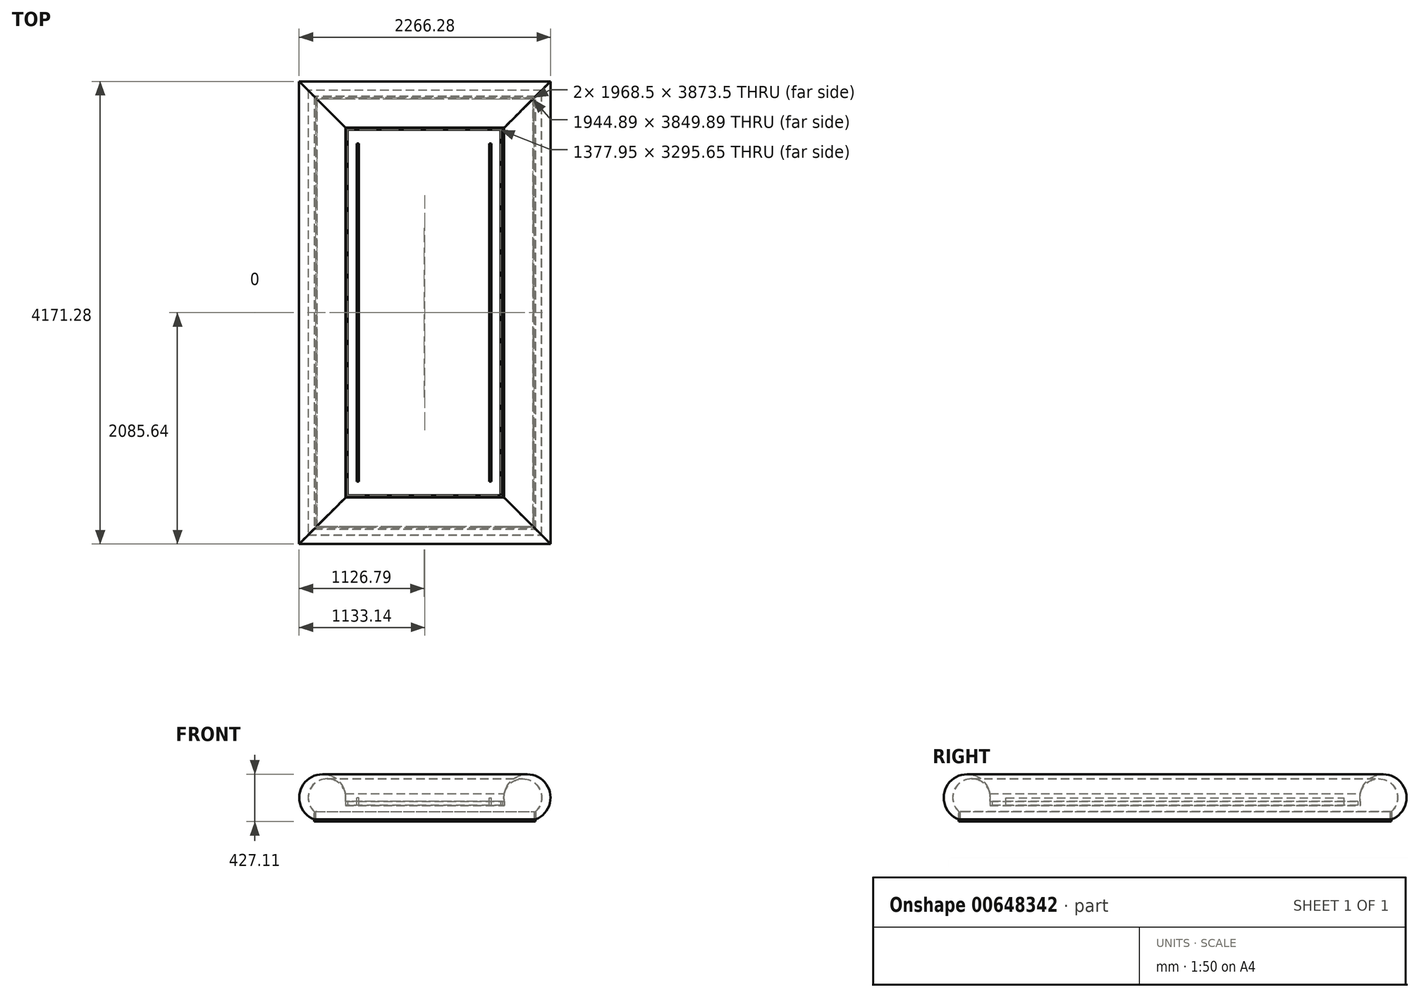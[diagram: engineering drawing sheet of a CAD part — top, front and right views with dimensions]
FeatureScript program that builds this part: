
annotation { "Feature Type Name" : "Feature", "Feature Type Description" : "" }
export const myFeature = defineFeature(function(context is Context, id is Id, definition is map)
    precondition{}
    {
        {
            var Q0;
            Q0=qCreatedBy(makeId("Front.planeOp"),FACE);
            var sketch = newSketch(context, id + "F0", { "sketchPlane" : qUnion([Q0])});
            skLineSegment(sketch, "E0.bottom", {"start": v(0, 0) * mm, "end": v(12.7, 0) * mm});
            skLineSegment(sketch, "E0.top", {"start": v(0, -88.9) * mm, "end": v(12.7, -88.9) * mm});
            skLineSegment(sketch, "E0.left", {"start": v(0, 0) * mm, "end": v(0, -88.9) * mm});
            skLineSegment(sketch, "E0.right", {"start": v(12.7, 0) * mm, "end": v(12.7, -88.9) * mm});
            skLineSegment(sketch, "E1.bottom", {"start": v(301.63, 57.15) * mm, "end": v(282.58, 57.15) * mm});
            skLineSegment(sketch, "E1.top", {"start": v(301.63, 92.07) * mm, "end": v(282.58, 92.07) * mm});
            skLineSegment(sketch, "E1.left", {"start": v(301.63, 57.15) * mm, "end": v(301.63, 92.08) * mm});
            skLineSegment(sketch, "E1.right", {"start": v(282.58, 57.15) * mm, "end": v(282.58, 92.08) * mm});
            skPoint(sketch, "E1.middle", {"position": v(292.1, 74.61) * mm});
            skArc(sketch, "E2", {"start": v(282.58, 92.08) * mm, "mid": v(61.68, 290.36) * mm, "end": v(0, 0) * mm});
            skLineSegment(sketch, "E3.bottom", {"start": v(403.23, 57.15) * mm, "end": v(384.18, 57.15) * mm});
            skLineSegment(sketch, "E3.top", {"start": v(403.23, 123.83) * mm, "end": v(384.18, 123.83) * mm});
            skLineSegment(sketch, "E3.left", {"start": v(403.23, 57.15) * mm, "end": v(403.23, 123.83) * mm});
            skLineSegment(sketch, "E3.right", {"start": v(384.18, 57.15) * mm, "end": v(384.18, 123.83) * mm});
            skPoint(sketch, "E3.middle", {"position": v(393.7, 90.49) * mm});
            skLineSegment(sketch, "E4", {"start": v(-111.56, 298.8) * mm, "end": v(114.8, 298.8) * mm});
            skArc(sketch, "E5", {"start": v(282.58, 92.08) * mm, "mid": v(-30.16, 310.3) * mm, "end": v(0, -69.85) * mm});
            skPoint(sketch, "E6", {"position": v(0, -44.45) * mm});
            skLineSegment(sketch, "E7", {"start": v(74.68, 338.21) * mm, "end": v(-177.95, 338.21) * mm});
            skLineSegment(sketch, "E8", {"start": v(990.6, 508.95) * mm, "end": v(990.6, -432.45) * mm, "construction": true});
            skLineSegment(sketch, "E9", {"start": v(12.7, 0) * mm, "end": v(282.58, 57.15) * mm});
            skLineSegment(sketch, "E10.MirrorCS", {"start": v(1679.58, 92.07) * mm, "end": v(1698.62, 92.07) * mm});
            skLineSegment(sketch, "E11.MirrorCS", {"start": v(1679.58, 57.15) * mm, "end": v(1679.58, 92.07) * mm});
            skLineSegment(sketch, "E12.MirrorCS", {"start": v(1577.97, 57.15) * mm, "end": v(1597.02, 57.15) * mm});
            skLineSegment(sketch, "E13.MirrorCS", {"start": v(1981.2, -88.9) * mm, "end": v(1968.5, -88.9) * mm});
            skLineSegment(sketch, "E14.MirrorCS", {"start": v(1679.58, 57.15) * mm, "end": v(1698.62, 57.15) * mm});
            skLineSegment(sketch, "E15.MirrorCS", {"start": v(1981.2, 0) * mm, "end": v(1968.5, 0) * mm});
            skLineSegment(sketch, "E16.MirrorCS", {"start": v(1698.62, 57.15) * mm, "end": v(1698.62, 92.08) * mm});
            skLineSegment(sketch, "E17.MirrorCS", {"start": v(1577.97, 123.83) * mm, "end": v(1597.02, 123.83) * mm});
            skLineSegment(sketch, "E18.MirrorCS", {"start": v(1968.5, 0) * mm, "end": v(1698.62, 57.15) * mm});
            skLineSegment(sketch, "E19.MirrorCS", {"start": v(1577.98, 57.15) * mm, "end": v(1577.98, 123.83) * mm});
            skLineSegment(sketch, "E20.MirrorCS", {"start": v(1597.02, 57.15) * mm, "end": v(1597.02, 123.83) * mm});
            skLineSegment(sketch, "E21.MirrorCS", {"start": v(1968.5, 0) * mm, "end": v(1968.5, -88.9) * mm});
            skLineSegment(sketch, "E22.MirrorCS", {"start": v(1981.2, 0) * mm, "end": v(1981.2, -88.9) * mm});
            skPoint(sketch, "E23.MirrorP", {"position": v(1981.2, -44.45) * mm});
            skArc(sketch, "E24.MirrorCS", {"start": v(1698.62, 92.08) * mm, "mid": v(2011.36, 310.3) * mm, "end": v(1981.2, -69.85) * mm});
            skArc(sketch, "E25.MirrorCS", {"start": v(1698.63, 92.08) * mm, "mid": v(1919.52, 290.36) * mm, "end": v(1981.2, 0) * mm});
            skPoint(sketch, "E26.MirrorP", {"position": v(1689.1, 74.61) * mm});
            skLineSegment(sketch, "E27.MirrorCS", {"start": v(1968.5, 0) * mm, "end": v(1968.5, 0) * mm});
            skPoint(sketch, "E28.MirrorP", {"position": v(1587.5, 90.49) * mm});
            skLineSegment(sketch, "E29.MirrorCS", {"start": v(1906.52, 338.21) * mm, "end": v(2159.15, 338.21) * mm});
            skLineSegment(sketch, "E30.MirrorCS", {"start": v(2092.76, 298.8) * mm, "end": v(1866.4, 298.8) * mm});
            skSolve(sketch);
        }
        {
            var Q0;
            Q0=qCreatedBy(makeId("Top.planeOp"),FACE);
            var sketch = newSketch(context, id + "F1", { "sketchPlane" : qUnion([Q0])});
            skLineSegment(sketch, "E31.bottom", {"start": v(6.35, 1943.1) * mm, "end": v(1987.55, 1943.1) * mm});
            skLineSegment(sketch, "E31.top", {"start": v(6.35, -1943.1) * mm, "end": v(1987.55, -1943.1) * mm});
            skLineSegment(sketch, "E31.left", {"start": v(6.35, 1943.1) * mm, "end": v(6.35, -1943.1) * mm});
            skLineSegment(sketch, "E31.right", {"start": v(1987.55, 1943.1) * mm, "end": v(1987.55, -1943.1) * mm});
            skLineSegment(sketch, "E32.bottom", {"start": v(1698.63, 1666.87) * mm, "end": v(282.58, 1666.87) * mm});
            skLineSegment(sketch, "E32.top", {"start": v(1698.63, -1666.87) * mm, "end": v(282.58, -1666.87) * mm});
            skLineSegment(sketch, "E32.left", {"start": v(1698.63, 1666.87) * mm, "end": v(1698.63, -1666.87) * mm});
            skLineSegment(sketch, "E32.right", {"start": v(282.58, 1666.87) * mm, "end": v(282.58, -1666.87) * mm});
            skPoint(sketch, "E32.middle", {"position": v(990.6, 0) * mm});
            skLineSegment(sketch, "E33.0", {"start": v(301.63, 0) * mm, "end": v(282.58, 0) * mm});
            skLineSegment(sketch, "E34.0", {"start": v(1679.58, 0) * mm, "end": v(1698.62, 0) * mm});
            skSolve(sketch);
        }
        {
            var Q0;
            {var subQ3=sQuery(id+"F0.wireOp",EDGE,"E0.bottom");Q0=makeQuery(id+"F0.imprint","IMPRINT",FACE,{"disambiguationData":[TD([[makeQuery(id+"F0.imprint","IMPRINT",EDGE,{"derivedFrom":subQ3}),-1.0]])]});}
            var Q1;
            Q1=sQuery(id+"F1.wireOp",EDGE,"E31.left");
            var Q2;
            Q2=sQuery(id+"F1.wireOp",EDGE,"E31.top");
            var Q3;
            Q3=sQuery(id+"F1.wireOp",EDGE,"E31.right");
            var Q4;
            Q4=sQuery(id+"F1.wireOp",EDGE,"E31.bottom");
            sweep(context, id + "F2", {"profiles" : qUnion([Q0]), "path" : qUnion([Q1, Q2, Q3, Q4])});
        }
        {
            var Q0;
            Q0=makeQuery(id+"F0.imprint","IMPRINT",FACE,{"disambiguationData":[TD([[makeQuery(id+"F0.imprint","IMPRINT",EDGE,{"derivedFrom":sQuery(id+"F0.wireOp",EDGE,"E12.MirrorCS")}),1.0]])]});
            var Q1;
            Q1=makeQuery(id+"F0.imprint","IMPRINT",FACE,{"disambiguationData":[TD([[makeQuery(id+"F0.imprint","IMPRINT",EDGE,{"derivedFrom":sQuery(id+"F0.wireOp",EDGE,"E3.bottom")}),-1.0]])]});
            extrude(context, id + "F3", {"entities" : qUnion([Q0, Q1]), "endBound" : BoundingType.SYMMETRIC, "depth" : 3048 * mm, "offsetDistance" : 25 * mm});
        }
        {
            var Q0;
            Q0=makeQuery(id+"F0.imprint","IMPRINT",FACE,{"disambiguationData":[TD([[makeQuery(id+"F0.imprint","IMPRINT",EDGE,{"derivedFrom":sQuery(id+"F0.wireOp",EDGE,"E1.bottom")}),-1.0]])]});
            var Q1;
            Q1=sQuery(id+"F1.wireOp",EDGE,"E32.right");
            var Q2;
            Q2=sQuery(id+"F1.wireOp",EDGE,"E32.top");
            var Q3;
            Q3=sQuery(id+"F1.wireOp",EDGE,"E32.left");
            var Q4;
            Q4=sQuery(id+"F1.wireOp",EDGE,"E32.bottom");
            sweep(context, id + "F4", {"profiles" : qUnion([Q0]), "path" : qUnion([Q1, Q2, Q3, Q4])});
        }
        {
            var Q0;
            {var subQ1=sQuery(id+"F0.wireOp",EDGE,"E0.bottom");Q0=makeQuery(id+"F0.imprint","IMPRINT",FACE,{"disambiguationData":[TD([[makeQuery(id+"F0.imprint","IMPRINT",EDGE,{"derivedFrom":subQ1}),1.0]])]});}
            var Q1;
            Q1=sQuery(id+"F1.wireOp",EDGE,"E31.left");
            var Q2;
            Q2=sQuery(id+"F1.wireOp",EDGE,"E31.top");
            var Q3;
            Q3=sQuery(id+"F1.wireOp",EDGE,"E31.right");
            var Q4;
            Q4=sQuery(id+"F1.wireOp",EDGE,"E31.bottom");
            sweep(context, id + "F5", {"profiles" : qUnion([Q0]), "path" : qUnion([Q1, Q2, Q3, Q4])});
        }
        {
            var Q0;
            {var subQ0=sQuery(id+"F0.wireOp",EDGE,"E2");var subQ5=sQuery(id+"F0.wireOp",EDGE,"E4");var subQ6=makeQuery(id+"F0.imprint","INTERSECT",VERTEX,{"derivedFrom":[subQ0,subQ5]});Q0=makeQuery(id+"F0.imprint","IMPRINT",FACE,{"disambiguationData":[TD([[makeQuery(id+"F0.imprint","IMPRINT",EDGE,{"disambiguationData":[TD([[subQ6,1.0]])],"derivedFrom":subQ5}),-1.0]])]});}
            var Q1;
            {var subQ3=sQuery(id+"F0.wireOp",EDGE,"E5");var subQ6=makeQuery(id+"F0.imprint","IMPRINT",VERTEX,{"derivedFrom":subQ3});Q1=makeQuery(id+"F0.imprint","IMPRINT",FACE,{"disambiguationData":[TD([[makeQuery(id+"F0.imprint","IMPRINT",EDGE,{"disambiguationData":[TD([[subQ6,1.0]])],"derivedFrom":subQ3}),1.0]])]});}
            var Q2;
            {var subQ1=sQuery(id+"F0.wireOp",EDGE,"E0.bottom");Q2=makeQuery(id+"F0.imprint","IMPRINT",FACE,{"disambiguationData":[TD([[makeQuery(id+"F0.imprint","IMPRINT",EDGE,{"derivedFrom":subQ1}),1.0]])]});}
            var Q3;
            Q3=sQuery(id+"F1.wireOp",EDGE,"E31.left");
            var Q4;
            Q4=sQuery(id+"F1.wireOp",EDGE,"E31.top");
            var Q5;
            Q5=sQuery(id+"F1.wireOp",EDGE,"E31.right");
            var Q6;
            Q6=sQuery(id+"F1.wireOp",EDGE,"E31.bottom");
            sweep(context, id + "F6", {"profiles" : qUnion([Q0, Q1, Q2]), "path" : qUnion([Q3, Q4, Q5, Q6])});
        }
        {
            var Q0;
            Q0=makeQuery(id+"F5.opSweep","SWEPT_FACE",FACE,{"disambiguationData":[OSD([sQuery(id+"F0.wireOp",EDGE,"E9"),sQuery(id+"F1.wireOp",EDGE,"E31.left")])]});
            var Q1;
            Q1=makeQuery(id+"F5.opSweep","SWEPT_FACE",FACE,{"disambiguationData":[OSD([sQuery(id+"F0.wireOp",EDGE,"E9"),sQuery(id+"F1.wireOp",EDGE,"E31.top")])]});
            var Q2;
            Q2=makeQuery(id+"F5.opSweep","SWEPT_FACE",FACE,{"disambiguationData":[OSD([sQuery(id+"F0.wireOp",EDGE,"E9"),sQuery(id+"F1.wireOp",EDGE,"E31.right")])]});
            var Q3;
            Q3=makeQuery(id+"F5.opSweep","SWEPT_FACE",FACE,{"disambiguationData":[OSD([sQuery(id+"F0.wireOp",EDGE,"E9"),sQuery(id+"F1.wireOp",EDGE,"E31.bottom")])]});
            shell(context, id + "F7", {"entities" : qUnion([Q0, Q1, Q2, Q3]), "thickness" : 2.5 * mm});
        }
        {
            var Q0;
            Q0=makeQuery(id+"F6.opSweep","SWEPT_FACE",FACE,{"disambiguationData":[OSD([sQuery(id+"F0.wireOp",EDGE,"E9"),sQuery(id+"F1.wireOp",EDGE,"E31.left")])]});
            var Q1;
            Q1=makeQuery(id+"F6.opSweep","SWEPT_FACE",FACE,{"disambiguationData":[OSD([sQuery(id+"F0.wireOp",EDGE,"E9"),sQuery(id+"F1.wireOp",EDGE,"E31.top")])]});
            var Q2;
            Q2=makeQuery(id+"F6.opSweep","SWEPT_FACE",FACE,{"disambiguationData":[OSD([sQuery(id+"F0.wireOp",EDGE,"E9"),sQuery(id+"F1.wireOp",EDGE,"E31.right")])]});
            var Q3;
            Q3=makeQuery(id+"F6.opSweep","SWEPT_FACE",FACE,{"disambiguationData":[OSD([sQuery(id+"F0.wireOp",EDGE,"E9"),sQuery(id+"F1.wireOp",EDGE,"E31.bottom")])]});
            shell(context, id + "F8", {"entities" : qUnion([Q0, Q1, Q2, Q3]), "thickness" : 2.5 * mm});
        }
    });
